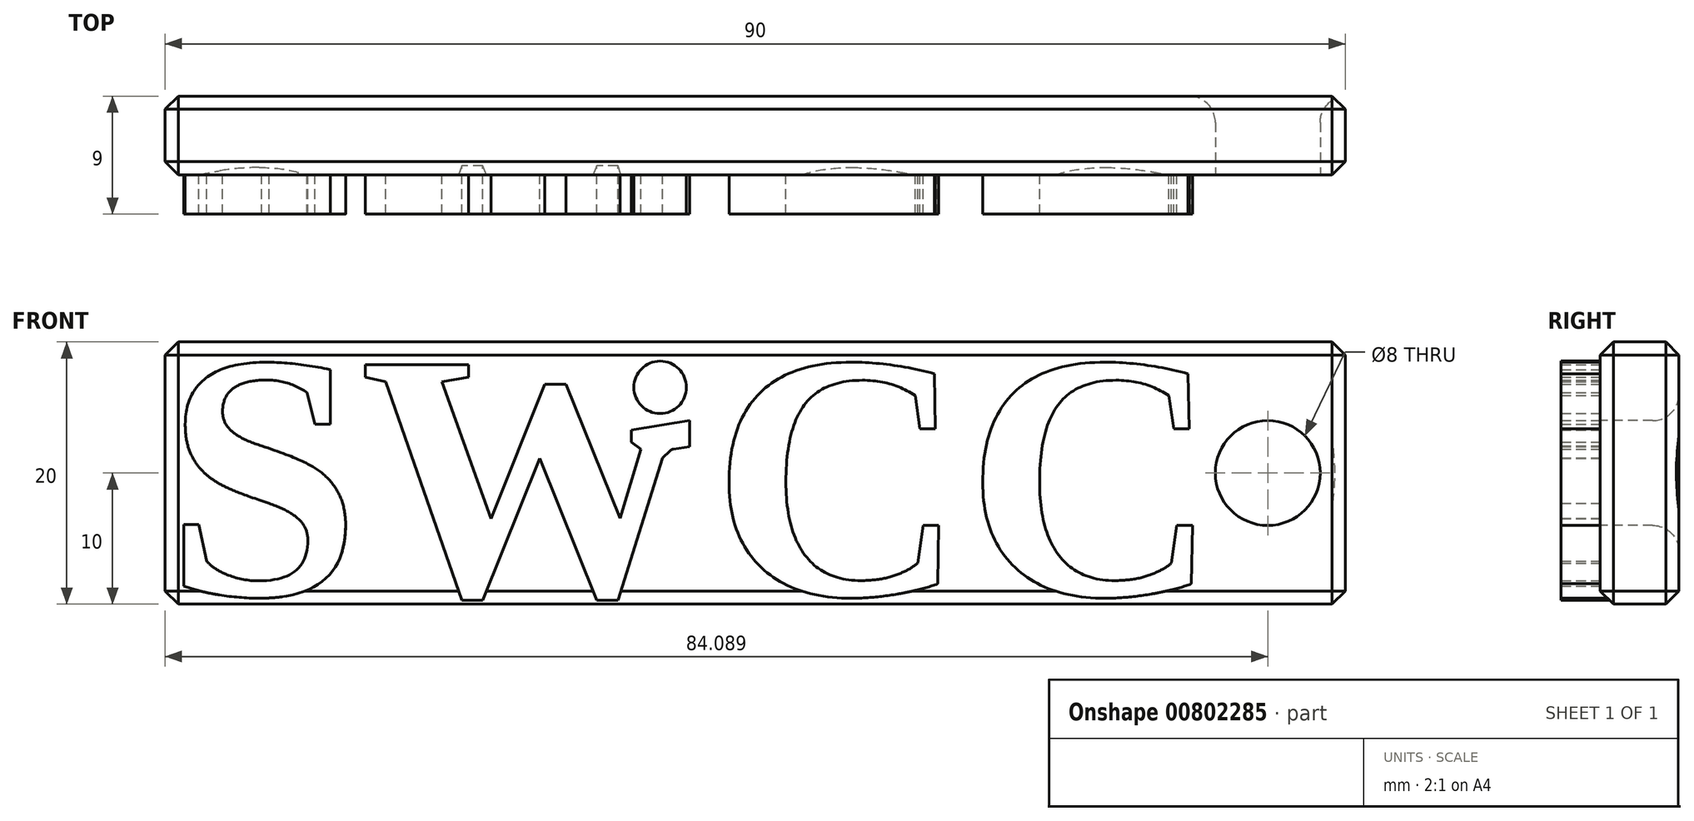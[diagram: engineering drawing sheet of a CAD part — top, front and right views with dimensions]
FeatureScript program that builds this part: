
annotation { "Feature Type Name" : "Feature", "Feature Type Description" : "" }
export const myFeature = defineFeature(function(context is Context, id is Id, definition is map)
    precondition{}
    {
        {
            var Q0;
            Q0=qCreatedBy(makeId("Front.planeOp"),FACE);
            var sketch = newSketch(context, id + "F0", { "sketchPlane" : qUnion([Q0])});
            skText(sketch, "E0", { "text": "SWCC", "fontName": "Tinos-Bold.ttf"});
            skLineSegment(sketch, "E1", {"start": v(0, 0) * mm, "end": v(0, -6) * mm});
            skLineSegment(sketch, "E2", {"start": v(0, -6) * mm, "end": v(-4.45, -6.71) * mm});
            skLineSegment(sketch, "E3", {"start": v(-4.45, -6.71) * mm, "end": v(-4.45, -7.65) * mm});
            skLineSegment(sketch, "E4", {"start": v(-4.45, -7.65) * mm, "end": v(-3.72, -8.2) * mm});
            skLineSegment(sketch, "E5", {"start": v(0, -6) * mm, "end": v(0, -8) * mm});
            skLineSegment(sketch, "E6", {"start": v(0, -8) * mm, "end": v(-1.23, -8.18) * mm});
            skLineSegment(sketch, "E7", {"start": v(-1.49, -8.3) * mm, "end": v(-2.55, -9.29) * mm});
            skLineSegment(sketch, "E8", {"start": v(-2.55, -9.29) * mm, "end": v(-3.72, -8.2) * mm});
            skPoint(sketch, "E9.visualSharp", {"position": v(-1.38, -8.2) * mm});
            skArc(sketch, "E9.filletArc", {"start": v(-1.23, -8.18) * mm, "mid": v(-1.37, -8.22) * mm, "end": v(-1.49, -8.3) * mm});
            const initialGuessF0  = {"E0": [-0.04, -0.01929, 1, 0, 0.01929]};
            skSetInitialGuess(sketch, initialGuessF0);
            skSolve(sketch);
        }
        {
            var Q0;
            Q0=makeQuery(id+"F0.imprint","IMPRINT",FACE,{"disambiguationData":[TD([[makeQuery(id+"F0.imprint","IMPRINT",EDGE,{"derivedFrom":sQuery(id+"F0.wireOp",EDGE,"E0.sketch_text.stroke-0")}),-1.0]])]});
            var Q1;
            {var subQ7=sQuery(id+"F0.wireOp",EDGE,"E0.sketch_text.stroke-29");Q1=makeQuery(id+"F0.imprint","IMPRINT",FACE,{"disambiguationData":[TD([[makeQuery(id+"F0.imprint","IMPRINT",EDGE,{"derivedFrom":subQ7}),-1.0]])]});}
            var Q2;
            {var subQ0=sQuery(id+"F0.wireOp",EDGE,"E8");Q2=makeQuery(id+"F0.imprint","IMPRINT",FACE,{"disambiguationData":[TD([[makeQuery(id+"F0.imprint","IMPRINT",EDGE,{"derivedFrom":subQ0}),-1.0]])]});}
            var Q3;
            {var subQ5=sQuery(id+"F0.wireOp",EDGE,"E3");Q3=makeQuery(id+"F0.imprint","IMPRINT",FACE,{"disambiguationData":[TD([[makeQuery(id+"F0.imprint","IMPRINT",EDGE,{"derivedFrom":subQ5}),1.0]])]});}
            var Q4;
            {var subQ0=sQuery(id+"F0.wireOp",EDGE,"E5");Q4=makeQuery(id+"F0.imprint","IMPRINT",FACE,{"disambiguationData":[TD([[makeQuery(id+"F0.imprint","IMPRINT",EDGE,{"derivedFrom":subQ0}),-1.0]])]});}
            var Q5;
            Q5=makeQuery(id+"F0.imprint","IMPRINT",FACE,{"disambiguationData":[TD([[makeQuery(id+"F0.imprint","IMPRINT",EDGE,{"derivedFrom":sQuery(id+"F0.wireOp",EDGE,"E0.sketch_text.stroke-50")}),-1.0]])]});
            var Q6;
            Q6=makeQuery(id+"F0.imprint","IMPRINT",FACE,{"disambiguationData":[TD([[makeQuery(id+"F0.imprint","IMPRINT",EDGE,{"derivedFrom":sQuery(id+"F0.wireOp",EDGE,"E0.sketch_text.stroke-70")}),-1.0]])]});
            extrude(context, id + "F1", {"entities" : qUnion([Q0, Q1, Q2, Q3, Q4, Q5, Q6]), "depth" : 3 * mm, "offsetDistance" : 25 * mm});
        }
        {
            var Q0;
            Q0=qCreatedBy(makeId("Front.planeOp"),FACE);
            var sketch = newSketch(context, id + "F2", { "sketchPlane" : qUnion([Q0])});
            skLineSegment(sketch, "E10", {"start": v(0, 0) * mm, "end": v(-40, 0) * mm});
            skLineSegment(sketch, "E11", {"start": v(-40, 0) * mm, "end": v(-40, -20) * mm});
            skLineSegment(sketch, "E12", {"start": v(-40, -20) * mm, "end": v(50, -20) * mm});
            skLineSegment(sketch, "E13", {"start": v(50, -20) * mm, "end": v(50, 0) * mm});
            skLineSegment(sketch, "E14", {"start": v(50, 0) * mm, "end": v(0, 0) * mm});
            skSolve(sketch);
        }
        {
            var Q0;
            Q0 = qSketchRegion(id + "F2", true);
            extrude(context, id + "F3", {"entities" : qUnion([Q0]), "operationType" : NewBodyOperationType.ADD, "oppositeDirection" : true, "depth" : 6 * mm, "offsetDistance" : 25 * mm});
        }
        {
            var Q0;
            Q0=makeQuery(id+"F3.opExtrude","CAP_FACE",FACE,{"disambiguationData":[OSD([sQuery(id+"F2.wireOp",EDGE,"E10"),sQuery(id+"F2.wireOp",EDGE,"E11"),sQuery(id+"F2.wireOp",EDGE,"E12"),sQuery(id+"F2.wireOp",EDGE,"E13"),sQuery(id+"F2.wireOp",EDGE,"E14")])],"isStart":true});
            var sketch = newSketch(context, id + "F4", { "sketchPlane" : qUnion([Q0])});
            skCircle(sketch, "E15", {"center": v(-2.25, -3.47) * mm, "radius": 2 * mm});
            skSolve(sketch);
        }
        {
            var Q0;
            Q0=makeQuery(id+"F4.imprint","IMPRINT",FACE,{"disambiguationData":[TD([[makeQuery(id+"F4.imprint","IMPRINT",EDGE,{"derivedFrom":sQuery(id+"F4.wireOp",EDGE,"E15")}),1.0]])]});
            extrude(context, id + "F5", {"entities" : qUnion([Q0]), "operationType" : NewBodyOperationType.ADD, "depth" : 3 * mm, "offsetDistance" : 25 * mm});
        }
        {
            var Q0;
            Q0=makeQuery(id+"F3.opExtrude","CAP_EDGE",EDGE,{"disambiguationData":[OSD([sQuery(id+"F2.wireOp",EDGE,"E10"),sQuery(id+"F2.wireOp",EDGE,"E14")])],"isStart":false});
            var Q1;
            Q1=makeQuery(id+"F3.opExtrude","CAP_EDGE",EDGE,{"disambiguationData":[OSD([sQuery(id+"F2.wireOp",EDGE,"E10"),sQuery(id+"F2.wireOp",EDGE,"E14")])],"isStart":true});
            var Q2;
            Q2=makeQuery(id+"F3.opExtrude","CAP_EDGE",EDGE,{"disambiguationData":[OSD([sQuery(id+"F2.wireOp",EDGE,"E11")])],"isStart":true});
            var Q3;
            Q3=makeQuery(id+"F3.opExtrude","CAP_EDGE",EDGE,{"disambiguationData":[OSD([sQuery(id+"F2.wireOp",EDGE,"E11")])],"isStart":false});
            var Q4;
            Q4=makeQuery(id+"F3.opExtrude","CAP_EDGE",EDGE,{"disambiguationData":[OSD([sQuery(id+"F2.wireOp",EDGE,"E13")])],"isStart":true});
            var Q5;
            Q5=makeQuery(id+"F3.opExtrude","CAP_EDGE",EDGE,{"disambiguationData":[OSD([sQuery(id+"F2.wireOp",EDGE,"E12")])],"isStart":true});
            var Q6;
            Q6=makeQuery(id+"F3.opExtrude","CAP_EDGE",EDGE,{"disambiguationData":[OSD([sQuery(id+"F2.wireOp",EDGE,"E12")])],"isStart":false});
            var Q7;
            Q7=makeQuery(id+"F3.opExtrude","CAP_EDGE",EDGE,{"disambiguationData":[OSD([sQuery(id+"F2.wireOp",EDGE,"E13")])],"isStart":false});
            var Q8;
            Q8=makeQuery(id+"F3.opExtrude","SWEPT_EDGE",EDGE,{"disambiguationData":[OSD([sQuery(id+"F2.wireOp",EDGE,"E12"),sQuery(id+"F2.wireOp",EDGE,"E13")])]});
            var Q9;
            Q9=makeQuery(id+"F3.opExtrude","SWEPT_EDGE",EDGE,{"disambiguationData":[OSD([sQuery(id+"F2.wireOp",EDGE,"E13"),sQuery(id+"F2.wireOp",EDGE,"E14")])]});
            var Q10;
            Q10=makeQuery(id+"F3.opExtrude","SWEPT_EDGE",EDGE,{"disambiguationData":[OSD([sQuery(id+"F2.wireOp",EDGE,"E11"),sQuery(id+"F2.wireOp",EDGE,"E12")])]});
            var Q11;
            Q11=makeQuery(id+"F3.opExtrude","SWEPT_EDGE",EDGE,{"disambiguationData":[OSD([sQuery(id+"F2.wireOp",EDGE,"E10"),sQuery(id+"F2.wireOp",EDGE,"E11")])]});
            chamfer(context, id + "F6", {"entities" : qUnion([Q0, Q1, Q2, Q3, Q4, Q5, Q6, Q7, Q8, Q9, Q10, Q11]), "width" : 1 * mm, "tangentPropagation" : true});
        }
        {
            var Q0;
            Q0=makeQuery(id+"F6.opChamfer","SPLIT",FACE,{"disambiguationData":[OD(1.0)],"derivedFrom":makeQuery(id+"F3.opExtrude","CAP_FACE",FACE,{"disambiguationData":[OSD([sQuery(id+"F2.wireOp",EDGE,"E10"),sQuery(id+"F2.wireOp",EDGE,"E11"),sQuery(id+"F2.wireOp",EDGE,"E12"),sQuery(id+"F2.wireOp",EDGE,"E13"),sQuery(id+"F2.wireOp",EDGE,"E14")])],"isStart":true})});
            var sketch = newSketch(context, id + "F7", { "sketchPlane" : qUnion([Q0])});
            skCircle(sketch, "E16", {"center": v(44.09, -10) * mm, "radius": 4 * mm});
            skPoint(sketch, "E17", {"position": v(49, -10) * mm});
            skSolve(sketch);
        }
        {
            var Q0;
            Q0 = qSketchRegion(id + "F7", true);
            extrude(context, id + "F8", {"entities" : qUnion([Q0]), "operationType" : NewBodyOperationType.REMOVE, "oppositeDirection" : true, "depth" : 25 * mm, "offsetDistance" : 25 * mm});
        }
        {
            var Q0;
            Q0=makeQuery(id+"F8.boolean.opBoolean","COPY",EDGE,{"derivedFrom":makeQuery(id+"F8.opExtrude","CAP_EDGE",EDGE,{"disambiguationData":[OSD([sQuery(id+"F7.wireOp",EDGE,"E16")])],"isStart":true})});
            var Q1;
            Q1=makeQuery(id+"F8.boolean.opBoolean","INTERSECT",EDGE,{"derivedFrom":[makeQuery(id+"F3.opExtrude","CAP_FACE",FACE,{"disambiguationData":[OSD([sQuery(id+"F2.wireOp",EDGE,"E10"),sQuery(id+"F2.wireOp",EDGE,"E11"),sQuery(id+"F2.wireOp",EDGE,"E12"),sQuery(id+"F2.wireOp",EDGE,"E13"),sQuery(id+"F2.wireOp",EDGE,"E14")])],"isStart":false}),makeQuery(id+"F8.opExtrude","SWEPT_FACE",FACE,{"disambiguationData":[OSD([sQuery(id+"F7.wireOp",EDGE,"E16")])]})]});
            fillet(context, id + "F9", {"entities" : qUnion([Q0, Q1]), "radius" : 2 * mm, "tangentPropagation" : true, "allowEdgeOverflow" : false});
        }
    });
